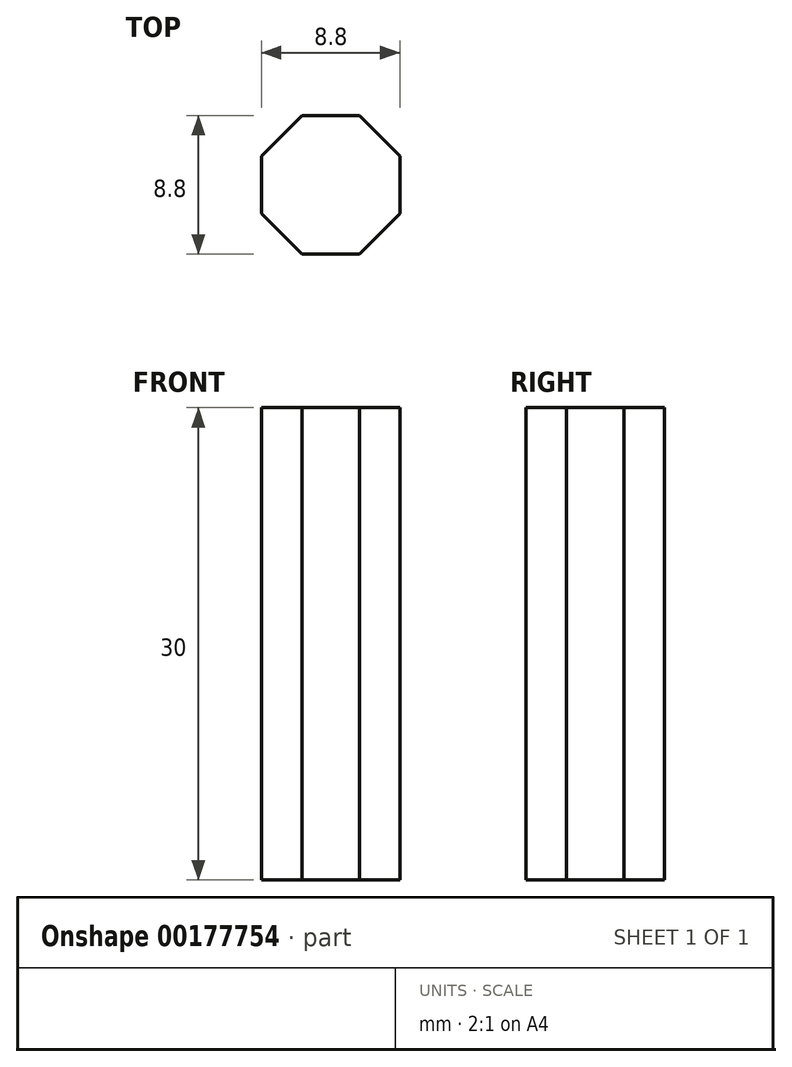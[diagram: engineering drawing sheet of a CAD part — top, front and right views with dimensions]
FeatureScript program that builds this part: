
annotation { "Feature Type Name" : "Feature", "Feature Type Description" : "" }
export const myFeature = defineFeature(function(context is Context, id is Id, definition is map)
    precondition{}
    {
        {
            var Q0;
            Q0=qCreatedBy(makeId("Top.planeOp"),FACE);
            var sketch = newSketch(context, id + "F0", { "sketchPlane" : qUnion([Q0])});
            skLineSegment(sketch, "E0", {"start": v(0, 0) * mm, "end": v(0, 17.05) * mm, "construction": true});
            skLineSegment(sketch, "E1", {"start": v(0, 17.05) * mm, "end": v(0, 0) * mm, "construction": true});
            skLineSegment(sketch, "E2", {"start": v(0, 0) * mm, "end": v(16.26, 0) * mm, "construction": true});
            skCircle(sketch, "E3.cCircle", {"center": v(0, 0) * mm, "radius": 4.4 * mm, "construction": true});
            skLineSegment(sketch, "E3.0", {"start": v(4.4, 1.82) * mm, "end": v(4.4, -1.82) * mm});
            skLineSegment(sketch, "E3.1", {"start": v(4.4, -1.82) * mm, "end": v(1.82, -4.4) * mm});
            skLineSegment(sketch, "E3.2", {"start": v(1.82, -4.4) * mm, "end": v(-1.82, -4.4) * mm});
            skLineSegment(sketch, "E3.3", {"start": v(-1.82, -4.4) * mm, "end": v(-4.4, -1.82) * mm});
            skLineSegment(sketch, "E3.4", {"start": v(-4.4, -1.82) * mm, "end": v(-4.4, 1.82) * mm});
            skLineSegment(sketch, "E3.5", {"start": v(-4.4, 1.82) * mm, "end": v(-1.82, 4.4) * mm});
            skLineSegment(sketch, "E3.6", {"start": v(-1.82, 4.4) * mm, "end": v(1.82, 4.4) * mm});
            skLineSegment(sketch, "E3.7", {"start": v(1.82, 4.4) * mm, "end": v(4.4, 1.82) * mm});
            skPoint(sketch, "E3.0.midPoint", {"position": v(4.4, 0) * mm});
            skSolve(sketch);
        }
        {
            var Q0;
            Q0 = qSketchRegion(id + "F0", true);
            extrude(context, id + "F1", {"entities" : qUnion([Q0]), "depth" : 30 * mm});
        }
    });
